# Revit family: VTp762 Фитинг разъемный PPR с переходом на ВР
name_source: partatom
category: Соединительные детали трубопроводов
revit_build: Autodesk Revit 2015 (Build: 20140606_1530(x64)
units: mm (PartAtom-declared; Revit-internal decimal feet)

## types (9) — shared parameters
Группа модели = VTp.700
Изготовитель = VALTEC S.R.L.
Коэффициент K = 0.5
Метод определения потерь = Коэффициент K
Описание = Фитинг разъемный PPR с переходом на внутр.резьбу
Таблица коэффициентов K = Angle Valve Threaded

## per-type parameters (varying)
| type | 20х1" | 20х1/2" | 20х3/4" | 25х1" | 25х3/4" | 32х1" | 40х1 1/4" | 50х1 1/2" | 63х2" | A | B | G | Lrez | d | Глубина вхождения | Код по классификатору |
| 20х1/2" | Нет | Да | Нет | Нет | Нет | Нет | Нет | Нет | Нет | 36 мм | 15 мм | 15 мм | 15 мм | 20 мм | 12 мм | VTp.762.0.02004 |
| 20х3/4" | Нет | Нет | Да | Нет | Нет | Нет | Нет | Нет | Нет | 41 мм | 15 мм | 20 мм | 15 мм | 20 мм | 12 мм | VTp.762.0.02005 |
| 20х1" | Да | Нет | Нет | Нет | Нет | Нет | Нет | Нет | Нет | 42 мм | 15 мм | 25 мм | 15 мм | 20 мм | 12 мм | VTp.762.0.02006 |
| 25х3/4" | Нет | Нет | Нет | Нет | Да | Нет | Нет | Нет | Нет | 41 мм | 18 мм | 20 мм | 15 мм | 25 мм | 12 мм | VTp.762.0.02505 |
| 40х1 1/4" | Нет | Нет | Нет | Нет | Нет | Нет | Да | Нет | Нет | 54 мм | 21 мм | 32 мм | 15 мм | 40 мм | 12 мм | VTp.762.0.04007 |
| 50х1 1/2" | Нет | Нет | Нет | Нет | Нет | Нет | Нет | Да | Нет | 61 мм | 24 мм | 40 мм | 15 мм | 50 мм | 12 мм | VTp.762.0.05008 |
| 32х1" | Нет | Нет | Нет | Нет | Нет | Да | Нет | Нет | Нет | 45 мм | 18 мм | 25 мм | 15 мм | 32 мм | 12 мм | VTp.762.0.03206 |
| 25х1" | Нет | Нет | Нет | Да | Нет | Нет | Нет | Нет | Нет | 42 мм | 18 мм | 25 мм | 15 мм | 25 мм | 12 мм | VTp.762.0.02506 |
| 63х2" | Нет | Нет | Нет | Нет | Нет | Нет | Нет | Нет | Да | 76 мм | 28 мм | 50 мм | 18 мм | 63 мм | 14 мм | VTp.762.0.06309 |
